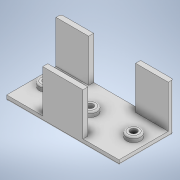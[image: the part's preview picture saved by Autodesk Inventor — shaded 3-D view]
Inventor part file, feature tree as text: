
AUTODESK INVENTOR PART (.ipt)
format: ipt  version: 2020 (Build 240168000, 168)  size: 238,080 bytes
history: native  units: in
note: dims shown in document units (in); Inventor stores cm internally (conversion verified against a paired STEP export)
features: extrude x11, sketch x11, fillet x2
ambient origin geometry x8: Origin, YZ Plane, XZ Plane, XY Plane, X Axis, Y Axis, Z Axis, Center Point
bodies: Solid1 (feature_tree)
feature tree (24):
  extrude  "Extrusion1"  Depth=1.2756in
  extrude  "Extrusion3"  Depth=0.1181in
  extrude  "Extrusion4"  Depth=1.0in TaperAngle=0.0deg
  extrude  "Extrusion5"  Depth=0.1181in TaperAngle=0.0deg
  extrude  "Extrusion6"  Depth=0.1181in TaperAngle=0.0deg
  extrude  "Extrusion9"  Depth=0.3346in
  extrude  "Extrusion10"  Depth=1.0236in
  extrude  "Extrusion11"  Depth=0.2953in
  extrude  "Extrusion14"  Depth=0.7677in
  fillet  "Fillet1"  Radius=0.1181in
  fillet  "Fillet2"  Radius=0.7677in
  extrude  "Extrusion15"  Depth=1.0in TaperAngle=0.0deg
  extrude  "Extrusion16"  Depth=0.0394in
  sketch  "Sketch1"  dims[d0=1.6142in d1=1.2756in]
  sketch  "Sketch3"  dims[d2=0.1181in d3=0.0in d8=0.1181in]
  sketch  "Sketch4"  dims[d9=0.1181in d10=1.0in d11=0.0in]
  sketch  "Sketch5"  dims[d12=0.8465in d13=0.1181in d14=0.0in]
  sketch  "Sketch6"  dims[d15=0.8465in d16=0.1181in d17=0.0in]
  sketch  "Sketch9"  dims[d20=0.3346in d21=0.3346in]
  sketch  "Sketch10"  dims[d22=0.1181in d23=0.0in d32=1.0236in]
  sketch  "Sketch11"  dims[d33=0.2953in d34=0.2953in]
  sketch  "Sketch14"  dims[d35=1.0236in d36=0.0in d37=0.3346in d38=0.1181in d39=0.0in d40=0.7677in]
  sketch  "Sketch15"  dims[d41=0.1181in d42=1.0in d43=0.0in]
  sketch  "Sketch16"  dims[d50=0.1772in d51=0.0in d52=0.0394in d53=0.0394in d54=0.1575in d55=0.1575in d56=0.1575in d57=0.3937in d58=0.0in d59=0.2362in d60=0.2362in d61=0.2362in d62=0.1181in d63=0.0in d44=0.0197in d45=0.0344in]
